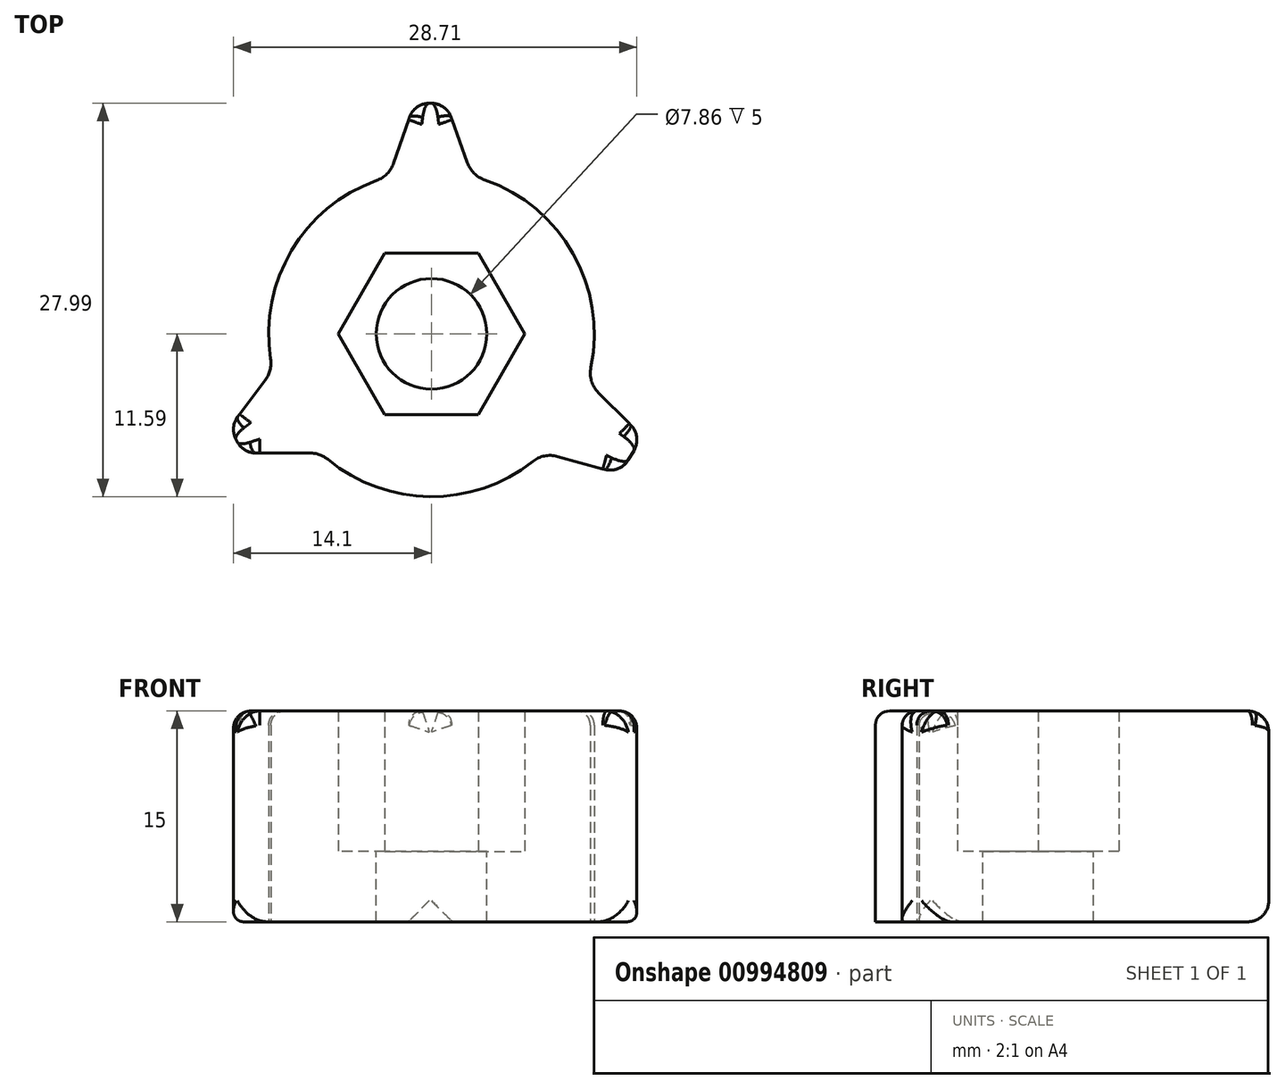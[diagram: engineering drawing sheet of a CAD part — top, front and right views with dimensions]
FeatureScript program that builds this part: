
annotation { "Feature Type Name" : "Feature", "Feature Type Description" : "" }
export const myFeature = defineFeature(function(context is Context, id is Id, definition is map)
    precondition{}
    {
        {
            var Q0;
            Q0=qCreatedBy(makeId("Top.planeOp"),FACE);
            var sketch = newSketch(context, id + "F0", { "sketchPlane" : qUnion([Q0])});
            skCircle(sketch, "E0.cCircle", {"center": v(0, 0) * mm, "radius": 5.75 * mm, "construction": true});
            skLineSegment(sketch, "E0.0", {"start": v(3.32, 5.75) * mm, "end": v(6.64, 0) * mm});
            skLineSegment(sketch, "E0.1", {"start": v(6.64, 0) * mm, "end": v(3.32, -5.75) * mm});
            skLineSegment(sketch, "E0.2", {"start": v(3.32, -5.75) * mm, "end": v(-3.32, -5.75) * mm});
            skLineSegment(sketch, "E0.3", {"start": v(-3.32, -5.75) * mm, "end": v(-6.64, 0) * mm});
            skLineSegment(sketch, "E0.4", {"start": v(-6.64, 0) * mm, "end": v(-3.32, 5.75) * mm});
            skLineSegment(sketch, "E0.5", {"start": v(-3.32, 5.75) * mm, "end": v(3.32, 5.75) * mm});
            skCircle(sketch, "E1", {"center": v(0, 0) * mm, "radius": 11.59 * mm});
            skLineSegment(sketch, "E2", {"start": v(-3.02, 11.19) * mm, "end": v(-1.23, 16.4) * mm});
            skLineSegment(sketch, "E3", {"start": v(-1.23, 16.4) * mm, "end": v(1.04, 16.4) * mm});
            skLineSegment(sketch, "E4", {"start": v(1.04, 16.4) * mm, "end": v(2.89, 11.22) * mm});
            skLineSegment(sketch, "E5", {"start": v(11.08, -3.4) * mm, "end": v(15, -7.3) * mm});
            skLineSegment(sketch, "E6", {"start": v(15, -7.3) * mm, "end": v(13.43, -9.95) * mm});
            skLineSegment(sketch, "E7", {"start": v(13.43, -9.95) * mm, "end": v(7.94, -8.44) * mm});
            skLineSegment(sketch, "E8", {"start": v(-7.9, -8.48) * mm, "end": v(-13.38, -8.48) * mm});
            skLineSegment(sketch, "E9", {"start": v(-13.38, -8.48) * mm, "end": v(-14.38, -6.67) * mm});
            skLineSegment(sketch, "E10", {"start": v(-14.38, -6.67) * mm, "end": v(-11.3, -2.58) * mm});
            skSolve(sketch);
        }
        {
            var Q0;
            Q0 = qSketchRegion(id + "F0", true);
            extrude(context, id + "F1", {"entities" : qUnion([Q0]), "depth" : 15 * mm, "offsetDistance" : 25 * mm});
        }
        {
            var Q0;
            Q0=makeQuery(id+"F0.imprint","IMPRINT",FACE,{"disambiguationData":[TD([[makeQuery(id+"F0.imprint","IMPRINT",EDGE,{"derivedFrom":sQuery(id+"F0.wireOp",EDGE,"E0.0")}),-1.0]])]});
            extrude(context, id + "F2", {"entities" : qUnion([Q0]), "operationType" : NewBodyOperationType.ADD, "depth" : 5 * mm, "offsetDistance" : 25 * mm});
        }
        {
            var Q0;
            Q0=makeQuery(id+"F2.opExtrude","CAP_FACE",FACE,{"disambiguationData":[OSD([sQuery(id+"F0.wireOp",EDGE,"E0.0"),sQuery(id+"F0.wireOp",EDGE,"E0.1"),sQuery(id+"F0.wireOp",EDGE,"E0.2"),sQuery(id+"F0.wireOp",EDGE,"E0.3"),sQuery(id+"F0.wireOp",EDGE,"E0.4"),sQuery(id+"F0.wireOp",EDGE,"E0.5")])],"isStart":false});
            var sketch = newSketch(context, id + "F3", { "sketchPlane" : qUnion([Q0])});
            skCircle(sketch, "E11", {"center": v(0, 0) * mm, "radius": 3.93 * mm});
            skSolve(sketch);
        }
        {
            var Q0;
            Q0=makeQuery(id+"F3.imprint","IMPRINT",FACE,{"disambiguationData":[TD([[makeQuery(id+"F3.imprint","IMPRINT",EDGE,{"derivedFrom":sQuery(id+"F3.wireOp",EDGE,"E11")}),1.0]])]});
            extrude(context, id + "F4", {"entities" : qUnion([Q0]), "operationType" : NewBodyOperationType.REMOVE, "endBound" : BoundingType.THROUGH_ALL, "oppositeDirection" : true, "depth" : 25 * mm, "offsetDistance" : 25 * mm});
        }
        {
            var Q0;
            Q0=makeQuery(id+"F1.opExtrude","SWEPT_EDGE",EDGE,{"disambiguationData":[OSD([sQuery(id+"F0.wireOp",EDGE,"wOrpiBWO-t8bo-ULgy-sOIL-iq1G5ipXFYLE"),sQuery(id+"F0.wireOp",EDGE,"E1")])]});
            var Q1;
            Q1=makeQuery(id+"F1.opExtrude","SWEPT_EDGE",EDGE,{"disambiguationData":[OSD([sQuery(id+"F0.wireOp",EDGE,"E1"),sQuery(id+"F0.wireOp",EDGE,"9cd6545f-047c-478b-9125-54586586866f")])]});
            var Q2;
            Q2=makeQuery(id+"F1.opExtrude","SWEPT_EDGE",EDGE,{"disambiguationData":[OSD([sQuery(id+"F0.wireOp",EDGE,"E1"),sQuery(id+"F0.wireOp",EDGE,"d0877aef-62f7-4734-ae38-8cc3c428e229")])]});
            var Q3;
            Q3=makeQuery(id+"F1.opExtrude","SWEPT_EDGE",EDGE,{"disambiguationData":[OSD([sQuery(id+"F0.wireOp",EDGE,"Ga7qppvu-lkfO-olbJ-rngz-mJgv76FKby2C"),sQuery(id+"F0.wireOp",EDGE,"E1")])]});
            var Q4;
            Q4=makeQuery(id+"F1.opExtrude","SWEPT_EDGE",EDGE,{"disambiguationData":[OSD([sQuery(id+"F0.wireOp",EDGE,"C5PBCUPG-eyh5-PjIv-aA1T-959jTYznR0oa"),sQuery(id+"F0.wireOp",EDGE,"E1")])]});
            var Q5;
            Q5=makeQuery(id+"F1.opExtrude","SWEPT_EDGE",EDGE,{"disambiguationData":[OSD([sQuery(id+"F0.wireOp",EDGE,"ubfB4LWy-1Tdm-pkzI-OJaf-DHBWXnkVYXMe"),sQuery(id+"F0.wireOp",EDGE,"E1")])]});
            fillet(context, id + "F5", {"entities" : qUnion([Q0, Q1, Q2, Q3, Q4, Q5]), "radius" : 2 * mm, "tangentPropagation" : true, "allowEdgeOverflow" : false});
        }
        {
            var Q0;
            {var subQ0=sQuery(id+"F0.wireOp",EDGE,"E1");var subQ1=sQuery(id+"F0.wireOp",EDGE,"wOrpiBWO-t8bo-ULgy-sOIL-iq1G5ipXFYLE");Q0=makeQuery(id+"F5.opFillet","BLEND_EDGE",EDGE,{"blendedFrom":[makeQuery(id+"F1.opExtrude","SWEPT_EDGE",EDGE,{"disambiguationData":[OSD([subQ1,subQ0])]}),makeQuery(id+"F1.opExtrude","CAP_FACE",FACE,{"disambiguationData":[OSD([sQuery(id+"F0.wireOp",EDGE,"E0.0"),sQuery(id+"F0.wireOp",EDGE,"E0.1"),sQuery(id+"F0.wireOp",EDGE,"E0.2"),sQuery(id+"F0.wireOp",EDGE,"E0.3"),sQuery(id+"F0.wireOp",EDGE,"E0.4"),sQuery(id+"F0.wireOp",EDGE,"E0.5"),subQ1,sQuery(id+"F0.wireOp",EDGE,"FlY8UkcK-kqYk-D5r6-5n9Y-Plu7moY1BHcf"),sQuery(id+"F0.wireOp",EDGE,"ubfB4LWy-1Tdm-pkzI-OJaf-DHBWXnkVYXMe"),sQuery(id+"F0.wireOp",EDGE,"C5PBCUPG-eyh5-PjIv-aA1T-959jTYznR0oa"),sQuery(id+"F0.wireOp",EDGE,"DOpIy9mY-4nxi-fRut-Ivpl-1Tq7dPj1OS8k"),sQuery(id+"F0.wireOp",EDGE,"Ga7qppvu-lkfO-olbJ-rngz-mJgv76FKby2C"),subQ0,sQuery(id+"F0.wireOp",EDGE,"d0877aef-62f7-4734-ae38-8cc3c428e229"),sQuery(id+"F0.wireOp",EDGE,"3b66b558-2be6-40e3-bff7-f227b0dd810b"),sQuery(id+"F0.wireOp",EDGE,"9cd6545f-047c-478b-9125-54586586866f")])],"isStart":false})],"blendedInto":[makeQuery(id+"F1.opExtrude","CAP_FACE",FACE,{"disambiguationData":[OSD([sQuery(id+"F0.wireOp",EDGE,"E0.0"),sQuery(id+"F0.wireOp",EDGE,"E0.1"),sQuery(id+"F0.wireOp",EDGE,"E0.2"),sQuery(id+"F0.wireOp",EDGE,"E0.3"),sQuery(id+"F0.wireOp",EDGE,"E0.4"),sQuery(id+"F0.wireOp",EDGE,"E0.5"),subQ1,sQuery(id+"F0.wireOp",EDGE,"FlY8UkcK-kqYk-D5r6-5n9Y-Plu7moY1BHcf"),sQuery(id+"F0.wireOp",EDGE,"ubfB4LWy-1Tdm-pkzI-OJaf-DHBWXnkVYXMe"),sQuery(id+"F0.wireOp",EDGE,"C5PBCUPG-eyh5-PjIv-aA1T-959jTYznR0oa"),sQuery(id+"F0.wireOp",EDGE,"DOpIy9mY-4nxi-fRut-Ivpl-1Tq7dPj1OS8k"),sQuery(id+"F0.wireOp",EDGE,"Ga7qppvu-lkfO-olbJ-rngz-mJgv76FKby2C"),subQ0,sQuery(id+"F0.wireOp",EDGE,"d0877aef-62f7-4734-ae38-8cc3c428e229"),sQuery(id+"F0.wireOp",EDGE,"3b66b558-2be6-40e3-bff7-f227b0dd810b"),sQuery(id+"F0.wireOp",EDGE,"9cd6545f-047c-478b-9125-54586586866f")])],"isStart":false})]});}
            var Q1;
            Q1=makeQuery(id+"F1.opExtrude","CAP_EDGE",EDGE,{"disambiguationData":[OSD([sQuery(id+"F0.wireOp",EDGE,"wOrpiBWO-t8bo-ULgy-sOIL-iq1G5ipXFYLE")])],"isStart":false});
            var Q2;
            {var subQ0=sQuery(id+"F0.wireOp",EDGE,"FlY8UkcK-kqYk-D5r6-5n9Y-Plu7moY1BHcf");var subQ1=sQuery(id+"F0.wireOp",EDGE,"wOrpiBWO-t8bo-ULgy-sOIL-iq1G5ipXFYLE");Q2=makeQuery(id+"Fg0UxEy2bN15xcL_1.opFillet","BLEND_EDGE",EDGE,{"blendedFrom":[makeQuery(id+"F1.opExtrude","SWEPT_EDGE",EDGE,{"disambiguationData":[OSD([subQ1,subQ0])]}),makeQuery(id+"F1.opExtrude","CAP_FACE",FACE,{"disambiguationData":[OSD([sQuery(id+"F0.wireOp",EDGE,"E0.0"),sQuery(id+"F0.wireOp",EDGE,"E0.1"),sQuery(id+"F0.wireOp",EDGE,"E0.2"),sQuery(id+"F0.wireOp",EDGE,"E0.3"),sQuery(id+"F0.wireOp",EDGE,"E0.4"),sQuery(id+"F0.wireOp",EDGE,"E0.5"),subQ1,subQ0,sQuery(id+"F0.wireOp",EDGE,"ubfB4LWy-1Tdm-pkzI-OJaf-DHBWXnkVYXMe"),sQuery(id+"F0.wireOp",EDGE,"C5PBCUPG-eyh5-PjIv-aA1T-959jTYznR0oa"),sQuery(id+"F0.wireOp",EDGE,"DOpIy9mY-4nxi-fRut-Ivpl-1Tq7dPj1OS8k"),sQuery(id+"F0.wireOp",EDGE,"Ga7qppvu-lkfO-olbJ-rngz-mJgv76FKby2C"),sQuery(id+"F0.wireOp",EDGE,"E1"),sQuery(id+"F0.wireOp",EDGE,"d0877aef-62f7-4734-ae38-8cc3c428e229"),sQuery(id+"F0.wireOp",EDGE,"3b66b558-2be6-40e3-bff7-f227b0dd810b"),sQuery(id+"F0.wireOp",EDGE,"9cd6545f-047c-478b-9125-54586586866f")])],"isStart":false})],"blendedInto":[makeQuery(id+"F1.opExtrude","CAP_FACE",FACE,{"disambiguationData":[OSD([sQuery(id+"F0.wireOp",EDGE,"E0.0"),sQuery(id+"F0.wireOp",EDGE,"E0.1"),sQuery(id+"F0.wireOp",EDGE,"E0.2"),sQuery(id+"F0.wireOp",EDGE,"E0.3"),sQuery(id+"F0.wireOp",EDGE,"E0.4"),sQuery(id+"F0.wireOp",EDGE,"E0.5"),subQ1,subQ0,sQuery(id+"F0.wireOp",EDGE,"ubfB4LWy-1Tdm-pkzI-OJaf-DHBWXnkVYXMe"),sQuery(id+"F0.wireOp",EDGE,"C5PBCUPG-eyh5-PjIv-aA1T-959jTYznR0oa"),sQuery(id+"F0.wireOp",EDGE,"DOpIy9mY-4nxi-fRut-Ivpl-1Tq7dPj1OS8k"),sQuery(id+"F0.wireOp",EDGE,"Ga7qppvu-lkfO-olbJ-rngz-mJgv76FKby2C"),sQuery(id+"F0.wireOp",EDGE,"E1"),sQuery(id+"F0.wireOp",EDGE,"d0877aef-62f7-4734-ae38-8cc3c428e229"),sQuery(id+"F0.wireOp",EDGE,"3b66b558-2be6-40e3-bff7-f227b0dd810b"),sQuery(id+"F0.wireOp",EDGE,"9cd6545f-047c-478b-9125-54586586866f")])],"isStart":false})]});}
            var Q3;
            Q3=makeQuery(id+"F1.opExtrude","CAP_EDGE",EDGE,{"disambiguationData":[OSD([sQuery(id+"F0.wireOp",EDGE,"FlY8UkcK-kqYk-D5r6-5n9Y-Plu7moY1BHcf")])],"isStart":false});
            var Q4;
            {var subQ0=sQuery(id+"F0.wireOp",EDGE,"ubfB4LWy-1Tdm-pkzI-OJaf-DHBWXnkVYXMe");var subQ1=sQuery(id+"F0.wireOp",EDGE,"FlY8UkcK-kqYk-D5r6-5n9Y-Plu7moY1BHcf");Q4=makeQuery(id+"Fg0UxEy2bN15xcL_1.opFillet","BLEND_EDGE",EDGE,{"blendedFrom":[makeQuery(id+"F1.opExtrude","SWEPT_EDGE",EDGE,{"disambiguationData":[OSD([subQ1,subQ0])]}),makeQuery(id+"F1.opExtrude","CAP_FACE",FACE,{"disambiguationData":[OSD([sQuery(id+"F0.wireOp",EDGE,"E0.0"),sQuery(id+"F0.wireOp",EDGE,"E0.1"),sQuery(id+"F0.wireOp",EDGE,"E0.2"),sQuery(id+"F0.wireOp",EDGE,"E0.3"),sQuery(id+"F0.wireOp",EDGE,"E0.4"),sQuery(id+"F0.wireOp",EDGE,"E0.5"),sQuery(id+"F0.wireOp",EDGE,"wOrpiBWO-t8bo-ULgy-sOIL-iq1G5ipXFYLE"),subQ1,subQ0,sQuery(id+"F0.wireOp",EDGE,"C5PBCUPG-eyh5-PjIv-aA1T-959jTYznR0oa"),sQuery(id+"F0.wireOp",EDGE,"DOpIy9mY-4nxi-fRut-Ivpl-1Tq7dPj1OS8k"),sQuery(id+"F0.wireOp",EDGE,"Ga7qppvu-lkfO-olbJ-rngz-mJgv76FKby2C"),sQuery(id+"F0.wireOp",EDGE,"E1"),sQuery(id+"F0.wireOp",EDGE,"d0877aef-62f7-4734-ae38-8cc3c428e229"),sQuery(id+"F0.wireOp",EDGE,"3b66b558-2be6-40e3-bff7-f227b0dd810b"),sQuery(id+"F0.wireOp",EDGE,"9cd6545f-047c-478b-9125-54586586866f")])],"isStart":false})],"blendedInto":[makeQuery(id+"F1.opExtrude","CAP_FACE",FACE,{"disambiguationData":[OSD([sQuery(id+"F0.wireOp",EDGE,"E0.0"),sQuery(id+"F0.wireOp",EDGE,"E0.1"),sQuery(id+"F0.wireOp",EDGE,"E0.2"),sQuery(id+"F0.wireOp",EDGE,"E0.3"),sQuery(id+"F0.wireOp",EDGE,"E0.4"),sQuery(id+"F0.wireOp",EDGE,"E0.5"),sQuery(id+"F0.wireOp",EDGE,"wOrpiBWO-t8bo-ULgy-sOIL-iq1G5ipXFYLE"),subQ1,subQ0,sQuery(id+"F0.wireOp",EDGE,"C5PBCUPG-eyh5-PjIv-aA1T-959jTYznR0oa"),sQuery(id+"F0.wireOp",EDGE,"DOpIy9mY-4nxi-fRut-Ivpl-1Tq7dPj1OS8k"),sQuery(id+"F0.wireOp",EDGE,"Ga7qppvu-lkfO-olbJ-rngz-mJgv76FKby2C"),sQuery(id+"F0.wireOp",EDGE,"E1"),sQuery(id+"F0.wireOp",EDGE,"d0877aef-62f7-4734-ae38-8cc3c428e229"),sQuery(id+"F0.wireOp",EDGE,"3b66b558-2be6-40e3-bff7-f227b0dd810b"),sQuery(id+"F0.wireOp",EDGE,"9cd6545f-047c-478b-9125-54586586866f")])],"isStart":false})]});}
            var Q5;
            Q5=makeQuery(id+"F1.opExtrude","CAP_EDGE",EDGE,{"disambiguationData":[OSD([sQuery(id+"F0.wireOp",EDGE,"ubfB4LWy-1Tdm-pkzI-OJaf-DHBWXnkVYXMe")])],"isStart":false});
            var Q6;
            {var subQ0=sQuery(id+"F0.wireOp",EDGE,"E1");var subQ1=sQuery(id+"F0.wireOp",EDGE,"ubfB4LWy-1Tdm-pkzI-OJaf-DHBWXnkVYXMe");Q6=makeQuery(id+"F5.opFillet","BLEND_EDGE",EDGE,{"blendedFrom":[makeQuery(id+"F1.opExtrude","SWEPT_EDGE",EDGE,{"disambiguationData":[OSD([subQ1,subQ0])]}),makeQuery(id+"F1.opExtrude","CAP_FACE",FACE,{"disambiguationData":[OSD([sQuery(id+"F0.wireOp",EDGE,"E0.0"),sQuery(id+"F0.wireOp",EDGE,"E0.1"),sQuery(id+"F0.wireOp",EDGE,"E0.2"),sQuery(id+"F0.wireOp",EDGE,"E0.3"),sQuery(id+"F0.wireOp",EDGE,"E0.4"),sQuery(id+"F0.wireOp",EDGE,"E0.5"),sQuery(id+"F0.wireOp",EDGE,"wOrpiBWO-t8bo-ULgy-sOIL-iq1G5ipXFYLE"),sQuery(id+"F0.wireOp",EDGE,"FlY8UkcK-kqYk-D5r6-5n9Y-Plu7moY1BHcf"),subQ1,sQuery(id+"F0.wireOp",EDGE,"C5PBCUPG-eyh5-PjIv-aA1T-959jTYznR0oa"),sQuery(id+"F0.wireOp",EDGE,"DOpIy9mY-4nxi-fRut-Ivpl-1Tq7dPj1OS8k"),sQuery(id+"F0.wireOp",EDGE,"Ga7qppvu-lkfO-olbJ-rngz-mJgv76FKby2C"),subQ0,sQuery(id+"F0.wireOp",EDGE,"d0877aef-62f7-4734-ae38-8cc3c428e229"),sQuery(id+"F0.wireOp",EDGE,"3b66b558-2be6-40e3-bff7-f227b0dd810b"),sQuery(id+"F0.wireOp",EDGE,"9cd6545f-047c-478b-9125-54586586866f")])],"isStart":false})],"blendedInto":[makeQuery(id+"F1.opExtrude","CAP_FACE",FACE,{"disambiguationData":[OSD([sQuery(id+"F0.wireOp",EDGE,"E0.0"),sQuery(id+"F0.wireOp",EDGE,"E0.1"),sQuery(id+"F0.wireOp",EDGE,"E0.2"),sQuery(id+"F0.wireOp",EDGE,"E0.3"),sQuery(id+"F0.wireOp",EDGE,"E0.4"),sQuery(id+"F0.wireOp",EDGE,"E0.5"),sQuery(id+"F0.wireOp",EDGE,"wOrpiBWO-t8bo-ULgy-sOIL-iq1G5ipXFYLE"),sQuery(id+"F0.wireOp",EDGE,"FlY8UkcK-kqYk-D5r6-5n9Y-Plu7moY1BHcf"),subQ1,sQuery(id+"F0.wireOp",EDGE,"C5PBCUPG-eyh5-PjIv-aA1T-959jTYznR0oa"),sQuery(id+"F0.wireOp",EDGE,"DOpIy9mY-4nxi-fRut-Ivpl-1Tq7dPj1OS8k"),sQuery(id+"F0.wireOp",EDGE,"Ga7qppvu-lkfO-olbJ-rngz-mJgv76FKby2C"),subQ0,sQuery(id+"F0.wireOp",EDGE,"d0877aef-62f7-4734-ae38-8cc3c428e229"),sQuery(id+"F0.wireOp",EDGE,"3b66b558-2be6-40e3-bff7-f227b0dd810b"),sQuery(id+"F0.wireOp",EDGE,"9cd6545f-047c-478b-9125-54586586866f")])],"isStart":false})]});}
            var Q7;
            {var subQ0=sQuery(id+"F0.wireOp",EDGE,"E1");Q7=makeQuery(id+"F1.opExtrude","CAP_EDGE",EDGE,{"disambiguationData":[OSD([subQ0]),TDD([makeQuery(id+"F0.imprint","IMPRINT",EDGE,{"disambiguationData":[TD([[makeQuery(id+"F0.imprint","INTERSECT",VERTEX,{"derivedFrom":[sQuery(id+"F0.wireOp",EDGE,"ubfB4LWy-1Tdm-pkzI-OJaf-DHBWXnkVYXMe"),subQ0]}),1.0]])],"derivedFrom":subQ0})])],"isStart":false});}
            var Q8;
            {var subQ0=sQuery(id+"F0.wireOp",EDGE,"E1");var subQ1=sQuery(id+"F0.wireOp",EDGE,"C5PBCUPG-eyh5-PjIv-aA1T-959jTYznR0oa");Q8=makeQuery(id+"F5.opFillet","BLEND_EDGE",EDGE,{"blendedFrom":[makeQuery(id+"F1.opExtrude","SWEPT_EDGE",EDGE,{"disambiguationData":[OSD([subQ1,subQ0])]}),makeQuery(id+"F1.opExtrude","CAP_FACE",FACE,{"disambiguationData":[OSD([sQuery(id+"F0.wireOp",EDGE,"E0.0"),sQuery(id+"F0.wireOp",EDGE,"E0.1"),sQuery(id+"F0.wireOp",EDGE,"E0.2"),sQuery(id+"F0.wireOp",EDGE,"E0.3"),sQuery(id+"F0.wireOp",EDGE,"E0.4"),sQuery(id+"F0.wireOp",EDGE,"E0.5"),sQuery(id+"F0.wireOp",EDGE,"wOrpiBWO-t8bo-ULgy-sOIL-iq1G5ipXFYLE"),sQuery(id+"F0.wireOp",EDGE,"FlY8UkcK-kqYk-D5r6-5n9Y-Plu7moY1BHcf"),sQuery(id+"F0.wireOp",EDGE,"ubfB4LWy-1Tdm-pkzI-OJaf-DHBWXnkVYXMe"),subQ1,sQuery(id+"F0.wireOp",EDGE,"DOpIy9mY-4nxi-fRut-Ivpl-1Tq7dPj1OS8k"),sQuery(id+"F0.wireOp",EDGE,"Ga7qppvu-lkfO-olbJ-rngz-mJgv76FKby2C"),subQ0,sQuery(id+"F0.wireOp",EDGE,"d0877aef-62f7-4734-ae38-8cc3c428e229"),sQuery(id+"F0.wireOp",EDGE,"3b66b558-2be6-40e3-bff7-f227b0dd810b"),sQuery(id+"F0.wireOp",EDGE,"9cd6545f-047c-478b-9125-54586586866f")])],"isStart":false})],"blendedInto":[makeQuery(id+"F1.opExtrude","CAP_FACE",FACE,{"disambiguationData":[OSD([sQuery(id+"F0.wireOp",EDGE,"E0.0"),sQuery(id+"F0.wireOp",EDGE,"E0.1"),sQuery(id+"F0.wireOp",EDGE,"E0.2"),sQuery(id+"F0.wireOp",EDGE,"E0.3"),sQuery(id+"F0.wireOp",EDGE,"E0.4"),sQuery(id+"F0.wireOp",EDGE,"E0.5"),sQuery(id+"F0.wireOp",EDGE,"wOrpiBWO-t8bo-ULgy-sOIL-iq1G5ipXFYLE"),sQuery(id+"F0.wireOp",EDGE,"FlY8UkcK-kqYk-D5r6-5n9Y-Plu7moY1BHcf"),sQuery(id+"F0.wireOp",EDGE,"ubfB4LWy-1Tdm-pkzI-OJaf-DHBWXnkVYXMe"),subQ1,sQuery(id+"F0.wireOp",EDGE,"DOpIy9mY-4nxi-fRut-Ivpl-1Tq7dPj1OS8k"),sQuery(id+"F0.wireOp",EDGE,"Ga7qppvu-lkfO-olbJ-rngz-mJgv76FKby2C"),subQ0,sQuery(id+"F0.wireOp",EDGE,"d0877aef-62f7-4734-ae38-8cc3c428e229"),sQuery(id+"F0.wireOp",EDGE,"3b66b558-2be6-40e3-bff7-f227b0dd810b"),sQuery(id+"F0.wireOp",EDGE,"9cd6545f-047c-478b-9125-54586586866f")])],"isStart":false})]});}
            var Q9;
            Q9=makeQuery(id+"F1.opExtrude","CAP_EDGE",EDGE,{"disambiguationData":[OSD([sQuery(id+"F0.wireOp",EDGE,"C5PBCUPG-eyh5-PjIv-aA1T-959jTYznR0oa")])],"isStart":false});
            var Q10;
            {var subQ0=sQuery(id+"F0.wireOp",EDGE,"DOpIy9mY-4nxi-fRut-Ivpl-1Tq7dPj1OS8k");var subQ1=sQuery(id+"F0.wireOp",EDGE,"C5PBCUPG-eyh5-PjIv-aA1T-959jTYznR0oa");Q10=makeQuery(id+"Fg0UxEy2bN15xcL_1.opFillet","BLEND_EDGE",EDGE,{"blendedFrom":[makeQuery(id+"F1.opExtrude","SWEPT_EDGE",EDGE,{"disambiguationData":[OSD([subQ1,subQ0])]}),makeQuery(id+"F1.opExtrude","CAP_FACE",FACE,{"disambiguationData":[OSD([sQuery(id+"F0.wireOp",EDGE,"E0.0"),sQuery(id+"F0.wireOp",EDGE,"E0.1"),sQuery(id+"F0.wireOp",EDGE,"E0.2"),sQuery(id+"F0.wireOp",EDGE,"E0.3"),sQuery(id+"F0.wireOp",EDGE,"E0.4"),sQuery(id+"F0.wireOp",EDGE,"E0.5"),sQuery(id+"F0.wireOp",EDGE,"wOrpiBWO-t8bo-ULgy-sOIL-iq1G5ipXFYLE"),sQuery(id+"F0.wireOp",EDGE,"FlY8UkcK-kqYk-D5r6-5n9Y-Plu7moY1BHcf"),sQuery(id+"F0.wireOp",EDGE,"ubfB4LWy-1Tdm-pkzI-OJaf-DHBWXnkVYXMe"),subQ1,subQ0,sQuery(id+"F0.wireOp",EDGE,"Ga7qppvu-lkfO-olbJ-rngz-mJgv76FKby2C"),sQuery(id+"F0.wireOp",EDGE,"E1"),sQuery(id+"F0.wireOp",EDGE,"d0877aef-62f7-4734-ae38-8cc3c428e229"),sQuery(id+"F0.wireOp",EDGE,"3b66b558-2be6-40e3-bff7-f227b0dd810b"),sQuery(id+"F0.wireOp",EDGE,"9cd6545f-047c-478b-9125-54586586866f")])],"isStart":false})],"blendedInto":[makeQuery(id+"F1.opExtrude","CAP_FACE",FACE,{"disambiguationData":[OSD([sQuery(id+"F0.wireOp",EDGE,"E0.0"),sQuery(id+"F0.wireOp",EDGE,"E0.1"),sQuery(id+"F0.wireOp",EDGE,"E0.2"),sQuery(id+"F0.wireOp",EDGE,"E0.3"),sQuery(id+"F0.wireOp",EDGE,"E0.4"),sQuery(id+"F0.wireOp",EDGE,"E0.5"),sQuery(id+"F0.wireOp",EDGE,"wOrpiBWO-t8bo-ULgy-sOIL-iq1G5ipXFYLE"),sQuery(id+"F0.wireOp",EDGE,"FlY8UkcK-kqYk-D5r6-5n9Y-Plu7moY1BHcf"),sQuery(id+"F0.wireOp",EDGE,"ubfB4LWy-1Tdm-pkzI-OJaf-DHBWXnkVYXMe"),subQ1,subQ0,sQuery(id+"F0.wireOp",EDGE,"Ga7qppvu-lkfO-olbJ-rngz-mJgv76FKby2C"),sQuery(id+"F0.wireOp",EDGE,"E1"),sQuery(id+"F0.wireOp",EDGE,"d0877aef-62f7-4734-ae38-8cc3c428e229"),sQuery(id+"F0.wireOp",EDGE,"3b66b558-2be6-40e3-bff7-f227b0dd810b"),sQuery(id+"F0.wireOp",EDGE,"9cd6545f-047c-478b-9125-54586586866f")])],"isStart":false})]});}
            var Q11;
            Q11=makeQuery(id+"F1.opExtrude","CAP_EDGE",EDGE,{"disambiguationData":[OSD([sQuery(id+"F0.wireOp",EDGE,"DOpIy9mY-4nxi-fRut-Ivpl-1Tq7dPj1OS8k")])],"isStart":false});
            var Q12;
            {var subQ0=sQuery(id+"F0.wireOp",EDGE,"Ga7qppvu-lkfO-olbJ-rngz-mJgv76FKby2C");var subQ1=sQuery(id+"F0.wireOp",EDGE,"DOpIy9mY-4nxi-fRut-Ivpl-1Tq7dPj1OS8k");Q12=makeQuery(id+"Fg0UxEy2bN15xcL_1.opFillet","BLEND_EDGE",EDGE,{"blendedFrom":[makeQuery(id+"F1.opExtrude","SWEPT_EDGE",EDGE,{"disambiguationData":[OSD([subQ1,subQ0])]}),makeQuery(id+"F1.opExtrude","CAP_FACE",FACE,{"disambiguationData":[OSD([sQuery(id+"F0.wireOp",EDGE,"E0.0"),sQuery(id+"F0.wireOp",EDGE,"E0.1"),sQuery(id+"F0.wireOp",EDGE,"E0.2"),sQuery(id+"F0.wireOp",EDGE,"E0.3"),sQuery(id+"F0.wireOp",EDGE,"E0.4"),sQuery(id+"F0.wireOp",EDGE,"E0.5"),sQuery(id+"F0.wireOp",EDGE,"wOrpiBWO-t8bo-ULgy-sOIL-iq1G5ipXFYLE"),sQuery(id+"F0.wireOp",EDGE,"FlY8UkcK-kqYk-D5r6-5n9Y-Plu7moY1BHcf"),sQuery(id+"F0.wireOp",EDGE,"ubfB4LWy-1Tdm-pkzI-OJaf-DHBWXnkVYXMe"),sQuery(id+"F0.wireOp",EDGE,"C5PBCUPG-eyh5-PjIv-aA1T-959jTYznR0oa"),subQ1,subQ0,sQuery(id+"F0.wireOp",EDGE,"E1"),sQuery(id+"F0.wireOp",EDGE,"d0877aef-62f7-4734-ae38-8cc3c428e229"),sQuery(id+"F0.wireOp",EDGE,"3b66b558-2be6-40e3-bff7-f227b0dd810b"),sQuery(id+"F0.wireOp",EDGE,"9cd6545f-047c-478b-9125-54586586866f")])],"isStart":false})],"blendedInto":[makeQuery(id+"F1.opExtrude","CAP_FACE",FACE,{"disambiguationData":[OSD([sQuery(id+"F0.wireOp",EDGE,"E0.0"),sQuery(id+"F0.wireOp",EDGE,"E0.1"),sQuery(id+"F0.wireOp",EDGE,"E0.2"),sQuery(id+"F0.wireOp",EDGE,"E0.3"),sQuery(id+"F0.wireOp",EDGE,"E0.4"),sQuery(id+"F0.wireOp",EDGE,"E0.5"),sQuery(id+"F0.wireOp",EDGE,"wOrpiBWO-t8bo-ULgy-sOIL-iq1G5ipXFYLE"),sQuery(id+"F0.wireOp",EDGE,"FlY8UkcK-kqYk-D5r6-5n9Y-Plu7moY1BHcf"),sQuery(id+"F0.wireOp",EDGE,"ubfB4LWy-1Tdm-pkzI-OJaf-DHBWXnkVYXMe"),sQuery(id+"F0.wireOp",EDGE,"C5PBCUPG-eyh5-PjIv-aA1T-959jTYznR0oa"),subQ1,subQ0,sQuery(id+"F0.wireOp",EDGE,"E1"),sQuery(id+"F0.wireOp",EDGE,"d0877aef-62f7-4734-ae38-8cc3c428e229"),sQuery(id+"F0.wireOp",EDGE,"3b66b558-2be6-40e3-bff7-f227b0dd810b"),sQuery(id+"F0.wireOp",EDGE,"9cd6545f-047c-478b-9125-54586586866f")])],"isStart":false})]});}
            var Q13;
            Q13=makeQuery(id+"F1.opExtrude","CAP_EDGE",EDGE,{"disambiguationData":[OSD([sQuery(id+"F0.wireOp",EDGE,"Ga7qppvu-lkfO-olbJ-rngz-mJgv76FKby2C")])],"isStart":false});
            var Q14;
            {var subQ0=sQuery(id+"F0.wireOp",EDGE,"E1");var subQ1=sQuery(id+"F0.wireOp",EDGE,"Ga7qppvu-lkfO-olbJ-rngz-mJgv76FKby2C");Q14=makeQuery(id+"F5.opFillet","BLEND_EDGE",EDGE,{"blendedFrom":[makeQuery(id+"F1.opExtrude","SWEPT_EDGE",EDGE,{"disambiguationData":[OSD([subQ1,subQ0])]}),makeQuery(id+"F1.opExtrude","CAP_FACE",FACE,{"disambiguationData":[OSD([sQuery(id+"F0.wireOp",EDGE,"E0.0"),sQuery(id+"F0.wireOp",EDGE,"E0.1"),sQuery(id+"F0.wireOp",EDGE,"E0.2"),sQuery(id+"F0.wireOp",EDGE,"E0.3"),sQuery(id+"F0.wireOp",EDGE,"E0.4"),sQuery(id+"F0.wireOp",EDGE,"E0.5"),sQuery(id+"F0.wireOp",EDGE,"wOrpiBWO-t8bo-ULgy-sOIL-iq1G5ipXFYLE"),sQuery(id+"F0.wireOp",EDGE,"FlY8UkcK-kqYk-D5r6-5n9Y-Plu7moY1BHcf"),sQuery(id+"F0.wireOp",EDGE,"ubfB4LWy-1Tdm-pkzI-OJaf-DHBWXnkVYXMe"),sQuery(id+"F0.wireOp",EDGE,"C5PBCUPG-eyh5-PjIv-aA1T-959jTYznR0oa"),sQuery(id+"F0.wireOp",EDGE,"DOpIy9mY-4nxi-fRut-Ivpl-1Tq7dPj1OS8k"),subQ1,subQ0,sQuery(id+"F0.wireOp",EDGE,"d0877aef-62f7-4734-ae38-8cc3c428e229"),sQuery(id+"F0.wireOp",EDGE,"3b66b558-2be6-40e3-bff7-f227b0dd810b"),sQuery(id+"F0.wireOp",EDGE,"9cd6545f-047c-478b-9125-54586586866f")])],"isStart":false})],"blendedInto":[makeQuery(id+"F1.opExtrude","CAP_FACE",FACE,{"disambiguationData":[OSD([sQuery(id+"F0.wireOp",EDGE,"E0.0"),sQuery(id+"F0.wireOp",EDGE,"E0.1"),sQuery(id+"F0.wireOp",EDGE,"E0.2"),sQuery(id+"F0.wireOp",EDGE,"E0.3"),sQuery(id+"F0.wireOp",EDGE,"E0.4"),sQuery(id+"F0.wireOp",EDGE,"E0.5"),sQuery(id+"F0.wireOp",EDGE,"wOrpiBWO-t8bo-ULgy-sOIL-iq1G5ipXFYLE"),sQuery(id+"F0.wireOp",EDGE,"FlY8UkcK-kqYk-D5r6-5n9Y-Plu7moY1BHcf"),sQuery(id+"F0.wireOp",EDGE,"ubfB4LWy-1Tdm-pkzI-OJaf-DHBWXnkVYXMe"),sQuery(id+"F0.wireOp",EDGE,"C5PBCUPG-eyh5-PjIv-aA1T-959jTYznR0oa"),sQuery(id+"F0.wireOp",EDGE,"DOpIy9mY-4nxi-fRut-Ivpl-1Tq7dPj1OS8k"),subQ1,subQ0,sQuery(id+"F0.wireOp",EDGE,"d0877aef-62f7-4734-ae38-8cc3c428e229"),sQuery(id+"F0.wireOp",EDGE,"3b66b558-2be6-40e3-bff7-f227b0dd810b"),sQuery(id+"F0.wireOp",EDGE,"9cd6545f-047c-478b-9125-54586586866f")])],"isStart":false})]});}
            var Q15;
            {var subQ0=sQuery(id+"F0.wireOp",EDGE,"E1");Q15=makeQuery(id+"F1.opExtrude","CAP_EDGE",EDGE,{"disambiguationData":[OSD([subQ0]),TDD([makeQuery(id+"F0.imprint","IMPRINT",EDGE,{"disambiguationData":[TD([[makeQuery(id+"F0.imprint","INTERSECT",VERTEX,{"derivedFrom":[sQuery(id+"F0.wireOp",EDGE,"Ga7qppvu-lkfO-olbJ-rngz-mJgv76FKby2C"),subQ0]}),1.0]])],"derivedFrom":subQ0})])],"isStart":false});}
            var Q16;
            {var subQ0=sQuery(id+"F0.wireOp",EDGE,"d0877aef-62f7-4734-ae38-8cc3c428e229");var subQ1=sQuery(id+"F0.wireOp",EDGE,"E1");Q16=makeQuery(id+"F5.opFillet","BLEND_EDGE",EDGE,{"blendedFrom":[makeQuery(id+"F1.opExtrude","SWEPT_EDGE",EDGE,{"disambiguationData":[OSD([subQ1,subQ0])]}),makeQuery(id+"F1.opExtrude","CAP_FACE",FACE,{"disambiguationData":[OSD([sQuery(id+"F0.wireOp",EDGE,"E0.0"),sQuery(id+"F0.wireOp",EDGE,"E0.1"),sQuery(id+"F0.wireOp",EDGE,"E0.2"),sQuery(id+"F0.wireOp",EDGE,"E0.3"),sQuery(id+"F0.wireOp",EDGE,"E0.4"),sQuery(id+"F0.wireOp",EDGE,"E0.5"),sQuery(id+"F0.wireOp",EDGE,"wOrpiBWO-t8bo-ULgy-sOIL-iq1G5ipXFYLE"),sQuery(id+"F0.wireOp",EDGE,"FlY8UkcK-kqYk-D5r6-5n9Y-Plu7moY1BHcf"),sQuery(id+"F0.wireOp",EDGE,"ubfB4LWy-1Tdm-pkzI-OJaf-DHBWXnkVYXMe"),sQuery(id+"F0.wireOp",EDGE,"C5PBCUPG-eyh5-PjIv-aA1T-959jTYznR0oa"),sQuery(id+"F0.wireOp",EDGE,"DOpIy9mY-4nxi-fRut-Ivpl-1Tq7dPj1OS8k"),sQuery(id+"F0.wireOp",EDGE,"Ga7qppvu-lkfO-olbJ-rngz-mJgv76FKby2C"),subQ1,subQ0,sQuery(id+"F0.wireOp",EDGE,"3b66b558-2be6-40e3-bff7-f227b0dd810b"),sQuery(id+"F0.wireOp",EDGE,"9cd6545f-047c-478b-9125-54586586866f")])],"isStart":false})],"blendedInto":[makeQuery(id+"F1.opExtrude","CAP_FACE",FACE,{"disambiguationData":[OSD([sQuery(id+"F0.wireOp",EDGE,"E0.0"),sQuery(id+"F0.wireOp",EDGE,"E0.1"),sQuery(id+"F0.wireOp",EDGE,"E0.2"),sQuery(id+"F0.wireOp",EDGE,"E0.3"),sQuery(id+"F0.wireOp",EDGE,"E0.4"),sQuery(id+"F0.wireOp",EDGE,"E0.5"),sQuery(id+"F0.wireOp",EDGE,"wOrpiBWO-t8bo-ULgy-sOIL-iq1G5ipXFYLE"),sQuery(id+"F0.wireOp",EDGE,"FlY8UkcK-kqYk-D5r6-5n9Y-Plu7moY1BHcf"),sQuery(id+"F0.wireOp",EDGE,"ubfB4LWy-1Tdm-pkzI-OJaf-DHBWXnkVYXMe"),sQuery(id+"F0.wireOp",EDGE,"C5PBCUPG-eyh5-PjIv-aA1T-959jTYznR0oa"),sQuery(id+"F0.wireOp",EDGE,"DOpIy9mY-4nxi-fRut-Ivpl-1Tq7dPj1OS8k"),sQuery(id+"F0.wireOp",EDGE,"Ga7qppvu-lkfO-olbJ-rngz-mJgv76FKby2C"),subQ1,subQ0,sQuery(id+"F0.wireOp",EDGE,"3b66b558-2be6-40e3-bff7-f227b0dd810b"),sQuery(id+"F0.wireOp",EDGE,"9cd6545f-047c-478b-9125-54586586866f")])],"isStart":false})]});}
            var Q17;
            Q17=makeQuery(id+"F1.opExtrude","CAP_EDGE",EDGE,{"disambiguationData":[OSD([sQuery(id+"F0.wireOp",EDGE,"d0877aef-62f7-4734-ae38-8cc3c428e229")])],"isStart":false});
            var Q18;
            {var subQ0=sQuery(id+"F0.wireOp",EDGE,"3b66b558-2be6-40e3-bff7-f227b0dd810b");var subQ1=sQuery(id+"F0.wireOp",EDGE,"d0877aef-62f7-4734-ae38-8cc3c428e229");Q18=makeQuery(id+"Fg0UxEy2bN15xcL_1.opFillet","BLEND_EDGE",EDGE,{"blendedFrom":[makeQuery(id+"F1.opExtrude","SWEPT_EDGE",EDGE,{"disambiguationData":[OSD([subQ1,subQ0])]}),makeQuery(id+"F1.opExtrude","CAP_FACE",FACE,{"disambiguationData":[OSD([sQuery(id+"F0.wireOp",EDGE,"E0.0"),sQuery(id+"F0.wireOp",EDGE,"E0.1"),sQuery(id+"F0.wireOp",EDGE,"E0.2"),sQuery(id+"F0.wireOp",EDGE,"E0.3"),sQuery(id+"F0.wireOp",EDGE,"E0.4"),sQuery(id+"F0.wireOp",EDGE,"E0.5"),sQuery(id+"F0.wireOp",EDGE,"wOrpiBWO-t8bo-ULgy-sOIL-iq1G5ipXFYLE"),sQuery(id+"F0.wireOp",EDGE,"FlY8UkcK-kqYk-D5r6-5n9Y-Plu7moY1BHcf"),sQuery(id+"F0.wireOp",EDGE,"ubfB4LWy-1Tdm-pkzI-OJaf-DHBWXnkVYXMe"),sQuery(id+"F0.wireOp",EDGE,"C5PBCUPG-eyh5-PjIv-aA1T-959jTYznR0oa"),sQuery(id+"F0.wireOp",EDGE,"DOpIy9mY-4nxi-fRut-Ivpl-1Tq7dPj1OS8k"),sQuery(id+"F0.wireOp",EDGE,"Ga7qppvu-lkfO-olbJ-rngz-mJgv76FKby2C"),sQuery(id+"F0.wireOp",EDGE,"E1"),subQ1,subQ0,sQuery(id+"F0.wireOp",EDGE,"9cd6545f-047c-478b-9125-54586586866f")])],"isStart":false})],"blendedInto":[makeQuery(id+"F1.opExtrude","CAP_FACE",FACE,{"disambiguationData":[OSD([sQuery(id+"F0.wireOp",EDGE,"E0.0"),sQuery(id+"F0.wireOp",EDGE,"E0.1"),sQuery(id+"F0.wireOp",EDGE,"E0.2"),sQuery(id+"F0.wireOp",EDGE,"E0.3"),sQuery(id+"F0.wireOp",EDGE,"E0.4"),sQuery(id+"F0.wireOp",EDGE,"E0.5"),sQuery(id+"F0.wireOp",EDGE,"wOrpiBWO-t8bo-ULgy-sOIL-iq1G5ipXFYLE"),sQuery(id+"F0.wireOp",EDGE,"FlY8UkcK-kqYk-D5r6-5n9Y-Plu7moY1BHcf"),sQuery(id+"F0.wireOp",EDGE,"ubfB4LWy-1Tdm-pkzI-OJaf-DHBWXnkVYXMe"),sQuery(id+"F0.wireOp",EDGE,"C5PBCUPG-eyh5-PjIv-aA1T-959jTYznR0oa"),sQuery(id+"F0.wireOp",EDGE,"DOpIy9mY-4nxi-fRut-Ivpl-1Tq7dPj1OS8k"),sQuery(id+"F0.wireOp",EDGE,"Ga7qppvu-lkfO-olbJ-rngz-mJgv76FKby2C"),sQuery(id+"F0.wireOp",EDGE,"E1"),subQ1,subQ0,sQuery(id+"F0.wireOp",EDGE,"9cd6545f-047c-478b-9125-54586586866f")])],"isStart":false})]});}
            var Q19;
            Q19=makeQuery(id+"F1.opExtrude","CAP_EDGE",EDGE,{"disambiguationData":[OSD([sQuery(id+"F0.wireOp",EDGE,"3b66b558-2be6-40e3-bff7-f227b0dd810b")])],"isStart":false});
            var Q20;
            {var subQ0=sQuery(id+"F0.wireOp",EDGE,"9cd6545f-047c-478b-9125-54586586866f");var subQ1=sQuery(id+"F0.wireOp",EDGE,"3b66b558-2be6-40e3-bff7-f227b0dd810b");Q20=makeQuery(id+"Fg0UxEy2bN15xcL_1.opFillet","BLEND_EDGE",EDGE,{"blendedFrom":[makeQuery(id+"F1.opExtrude","SWEPT_EDGE",EDGE,{"disambiguationData":[OSD([subQ1,subQ0])]}),makeQuery(id+"F1.opExtrude","CAP_FACE",FACE,{"disambiguationData":[OSD([sQuery(id+"F0.wireOp",EDGE,"E0.0"),sQuery(id+"F0.wireOp",EDGE,"E0.1"),sQuery(id+"F0.wireOp",EDGE,"E0.2"),sQuery(id+"F0.wireOp",EDGE,"E0.3"),sQuery(id+"F0.wireOp",EDGE,"E0.4"),sQuery(id+"F0.wireOp",EDGE,"E0.5"),sQuery(id+"F0.wireOp",EDGE,"wOrpiBWO-t8bo-ULgy-sOIL-iq1G5ipXFYLE"),sQuery(id+"F0.wireOp",EDGE,"FlY8UkcK-kqYk-D5r6-5n9Y-Plu7moY1BHcf"),sQuery(id+"F0.wireOp",EDGE,"ubfB4LWy-1Tdm-pkzI-OJaf-DHBWXnkVYXMe"),sQuery(id+"F0.wireOp",EDGE,"C5PBCUPG-eyh5-PjIv-aA1T-959jTYznR0oa"),sQuery(id+"F0.wireOp",EDGE,"DOpIy9mY-4nxi-fRut-Ivpl-1Tq7dPj1OS8k"),sQuery(id+"F0.wireOp",EDGE,"Ga7qppvu-lkfO-olbJ-rngz-mJgv76FKby2C"),sQuery(id+"F0.wireOp",EDGE,"E1"),sQuery(id+"F0.wireOp",EDGE,"d0877aef-62f7-4734-ae38-8cc3c428e229"),subQ1,subQ0])],"isStart":false})],"blendedInto":[makeQuery(id+"F1.opExtrude","CAP_FACE",FACE,{"disambiguationData":[OSD([sQuery(id+"F0.wireOp",EDGE,"E0.0"),sQuery(id+"F0.wireOp",EDGE,"E0.1"),sQuery(id+"F0.wireOp",EDGE,"E0.2"),sQuery(id+"F0.wireOp",EDGE,"E0.3"),sQuery(id+"F0.wireOp",EDGE,"E0.4"),sQuery(id+"F0.wireOp",EDGE,"E0.5"),sQuery(id+"F0.wireOp",EDGE,"wOrpiBWO-t8bo-ULgy-sOIL-iq1G5ipXFYLE"),sQuery(id+"F0.wireOp",EDGE,"FlY8UkcK-kqYk-D5r6-5n9Y-Plu7moY1BHcf"),sQuery(id+"F0.wireOp",EDGE,"ubfB4LWy-1Tdm-pkzI-OJaf-DHBWXnkVYXMe"),sQuery(id+"F0.wireOp",EDGE,"C5PBCUPG-eyh5-PjIv-aA1T-959jTYznR0oa"),sQuery(id+"F0.wireOp",EDGE,"DOpIy9mY-4nxi-fRut-Ivpl-1Tq7dPj1OS8k"),sQuery(id+"F0.wireOp",EDGE,"Ga7qppvu-lkfO-olbJ-rngz-mJgv76FKby2C"),sQuery(id+"F0.wireOp",EDGE,"E1"),sQuery(id+"F0.wireOp",EDGE,"d0877aef-62f7-4734-ae38-8cc3c428e229"),subQ1,subQ0])],"isStart":false})]});}
            var Q21;
            Q21=makeQuery(id+"F1.opExtrude","CAP_EDGE",EDGE,{"disambiguationData":[OSD([sQuery(id+"F0.wireOp",EDGE,"9cd6545f-047c-478b-9125-54586586866f")])],"isStart":false});
            var Q22;
            {var subQ0=sQuery(id+"F0.wireOp",EDGE,"9cd6545f-047c-478b-9125-54586586866f");var subQ1=sQuery(id+"F0.wireOp",EDGE,"E1");Q22=makeQuery(id+"F5.opFillet","BLEND_EDGE",EDGE,{"blendedFrom":[makeQuery(id+"F1.opExtrude","SWEPT_EDGE",EDGE,{"disambiguationData":[OSD([subQ1,subQ0])]}),makeQuery(id+"F1.opExtrude","CAP_FACE",FACE,{"disambiguationData":[OSD([sQuery(id+"F0.wireOp",EDGE,"E0.0"),sQuery(id+"F0.wireOp",EDGE,"E0.1"),sQuery(id+"F0.wireOp",EDGE,"E0.2"),sQuery(id+"F0.wireOp",EDGE,"E0.3"),sQuery(id+"F0.wireOp",EDGE,"E0.4"),sQuery(id+"F0.wireOp",EDGE,"E0.5"),sQuery(id+"F0.wireOp",EDGE,"wOrpiBWO-t8bo-ULgy-sOIL-iq1G5ipXFYLE"),sQuery(id+"F0.wireOp",EDGE,"FlY8UkcK-kqYk-D5r6-5n9Y-Plu7moY1BHcf"),sQuery(id+"F0.wireOp",EDGE,"ubfB4LWy-1Tdm-pkzI-OJaf-DHBWXnkVYXMe"),sQuery(id+"F0.wireOp",EDGE,"C5PBCUPG-eyh5-PjIv-aA1T-959jTYznR0oa"),sQuery(id+"F0.wireOp",EDGE,"DOpIy9mY-4nxi-fRut-Ivpl-1Tq7dPj1OS8k"),sQuery(id+"F0.wireOp",EDGE,"Ga7qppvu-lkfO-olbJ-rngz-mJgv76FKby2C"),subQ1,sQuery(id+"F0.wireOp",EDGE,"d0877aef-62f7-4734-ae38-8cc3c428e229"),sQuery(id+"F0.wireOp",EDGE,"3b66b558-2be6-40e3-bff7-f227b0dd810b"),subQ0])],"isStart":false})],"blendedInto":[makeQuery(id+"F1.opExtrude","CAP_FACE",FACE,{"disambiguationData":[OSD([sQuery(id+"F0.wireOp",EDGE,"E0.0"),sQuery(id+"F0.wireOp",EDGE,"E0.1"),sQuery(id+"F0.wireOp",EDGE,"E0.2"),sQuery(id+"F0.wireOp",EDGE,"E0.3"),sQuery(id+"F0.wireOp",EDGE,"E0.4"),sQuery(id+"F0.wireOp",EDGE,"E0.5"),sQuery(id+"F0.wireOp",EDGE,"wOrpiBWO-t8bo-ULgy-sOIL-iq1G5ipXFYLE"),sQuery(id+"F0.wireOp",EDGE,"FlY8UkcK-kqYk-D5r6-5n9Y-Plu7moY1BHcf"),sQuery(id+"F0.wireOp",EDGE,"ubfB4LWy-1Tdm-pkzI-OJaf-DHBWXnkVYXMe"),sQuery(id+"F0.wireOp",EDGE,"C5PBCUPG-eyh5-PjIv-aA1T-959jTYznR0oa"),sQuery(id+"F0.wireOp",EDGE,"DOpIy9mY-4nxi-fRut-Ivpl-1Tq7dPj1OS8k"),sQuery(id+"F0.wireOp",EDGE,"Ga7qppvu-lkfO-olbJ-rngz-mJgv76FKby2C"),subQ1,sQuery(id+"F0.wireOp",EDGE,"d0877aef-62f7-4734-ae38-8cc3c428e229"),sQuery(id+"F0.wireOp",EDGE,"3b66b558-2be6-40e3-bff7-f227b0dd810b"),subQ0])],"isStart":false})]});}
            var Q23;
            {var subQ0=sQuery(id+"F0.wireOp",EDGE,"E1");Q23=makeQuery(id+"F1.opExtrude","CAP_EDGE",EDGE,{"disambiguationData":[OSD([subQ0]),TDD([makeQuery(id+"F0.imprint","IMPRINT",EDGE,{"disambiguationData":[TD([[makeQuery(id+"F0.imprint","INTERSECT",VERTEX,{"derivedFrom":[sQuery(id+"F0.wireOp",EDGE,"wOrpiBWO-t8bo-ULgy-sOIL-iq1G5ipXFYLE"),subQ0]}),-1.0]])],"derivedFrom":subQ0})])],"isStart":false});}
            fillet(context, id + "F6", {"entities" : qUnion([Q0, Q1, Q2, Q3, Q4, Q5, Q6, Q7, Q8, Q9, Q10, Q11, Q12, Q13, Q14, Q15, Q16, Q17, Q18, Q19, Q20, Q21, Q22, Q23]), "radius" : 1 * mm, "tangentPropagation" : true, "allowEdgeOverflow" : false});
        }
        {
            var Q0;
            Q0=makeQuery(id+"F1.opExtrude","SWEPT_FACE",FACE,{"disambiguationData":[OSD([sQuery(id+"F0.wireOp",EDGE,"E6")])]});
            var Q1;
            Q1=makeQuery(id+"F1.opExtrude","SWEPT_FACE",FACE,{"disambiguationData":[OSD([sQuery(id+"F0.wireOp",EDGE,"E3")])]});
            var Q2;
            Q2=makeQuery(id+"F1.opExtrude","SWEPT_FACE",FACE,{"disambiguationData":[OSD([sQuery(id+"F0.wireOp",EDGE,"E9")])]});
            fillet(context, id + "F7", {"entities" : qUnion([Q0, Q1, Q2]), "radius" : 1.5 * mm, "tangentPropagation" : true, "allowEdgeOverflow" : false});
        }
    });
